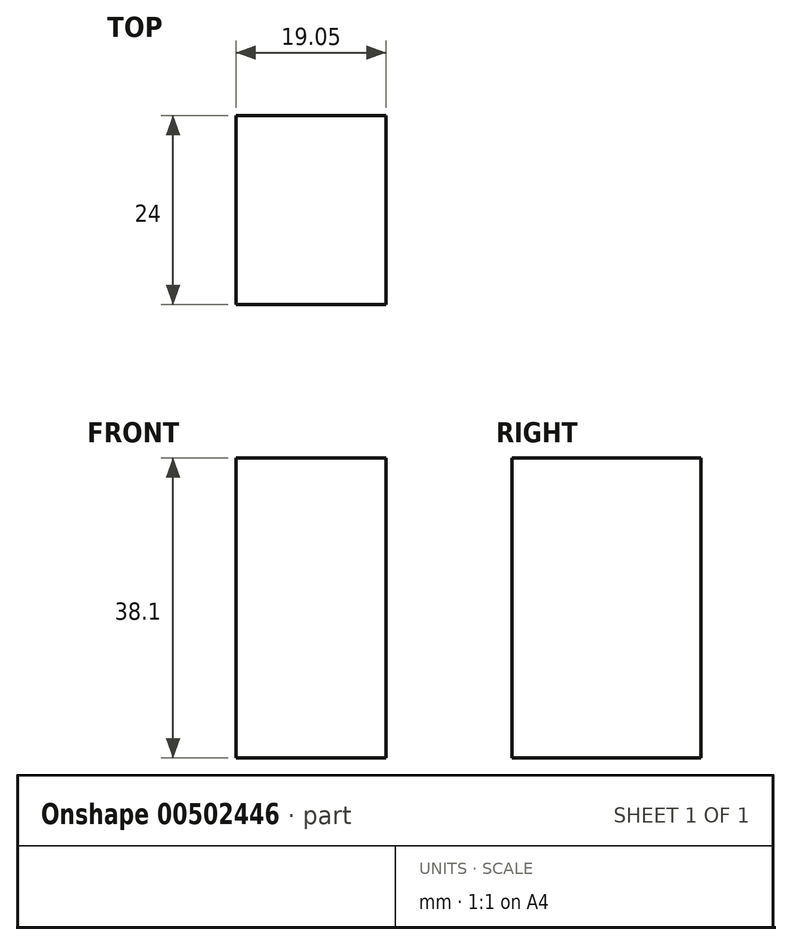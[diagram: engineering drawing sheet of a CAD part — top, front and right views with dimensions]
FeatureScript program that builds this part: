
annotation { "Feature Type Name" : "Feature", "Feature Type Description" : "" }
export const myFeature = defineFeature(function(context is Context, id is Id, definition is map)
    precondition{}
    {
        {
            assignVariable(context, id + "F0", {"name" : "BaseSide", "anyValue" : 27});
        }
        {
            var Q0;
            Q0=qCreatedBy(makeId("Front.planeOp"),FACE);
            var sketch = newSketch(context, id + "F1", { "sketchPlane" : qUnion([Q0])});
            skLineSegment(sketch, "E0.bottom", {"start": v(0, 38.1) * mm, "end": v(19.05, 38.1) * mm});
            skLineSegment(sketch, "E0.top", {"start": v(0, 0) * mm, "end": v(19.05, 0) * mm});
            skLineSegment(sketch, "E0.left", {"start": v(0, 38.1) * mm, "end": v(0, 0) * mm});
            skLineSegment(sketch, "E0.right", {"start": v(19.05, 38.1) * mm, "end": v(19.05, 0) * mm});
            skSolve(sketch);
        }
        {
            var Q0;
            Q0=makeQuery(id+"F1.imprint","IMPRINT",FACE,{"disambiguationData":[TD([[makeQuery(id+"F1.imprint","IMPRINT",EDGE,{"derivedFrom":sQuery(id+"F1.wireOp",EDGE,"E0.bottom")}),-1.0]])]});
            extrude(context, id + "F2", {"entities" : qUnion([Q0]), "depth" : (getVariable(context, 'BaseSide') - 3) * mm});
        }
    });
